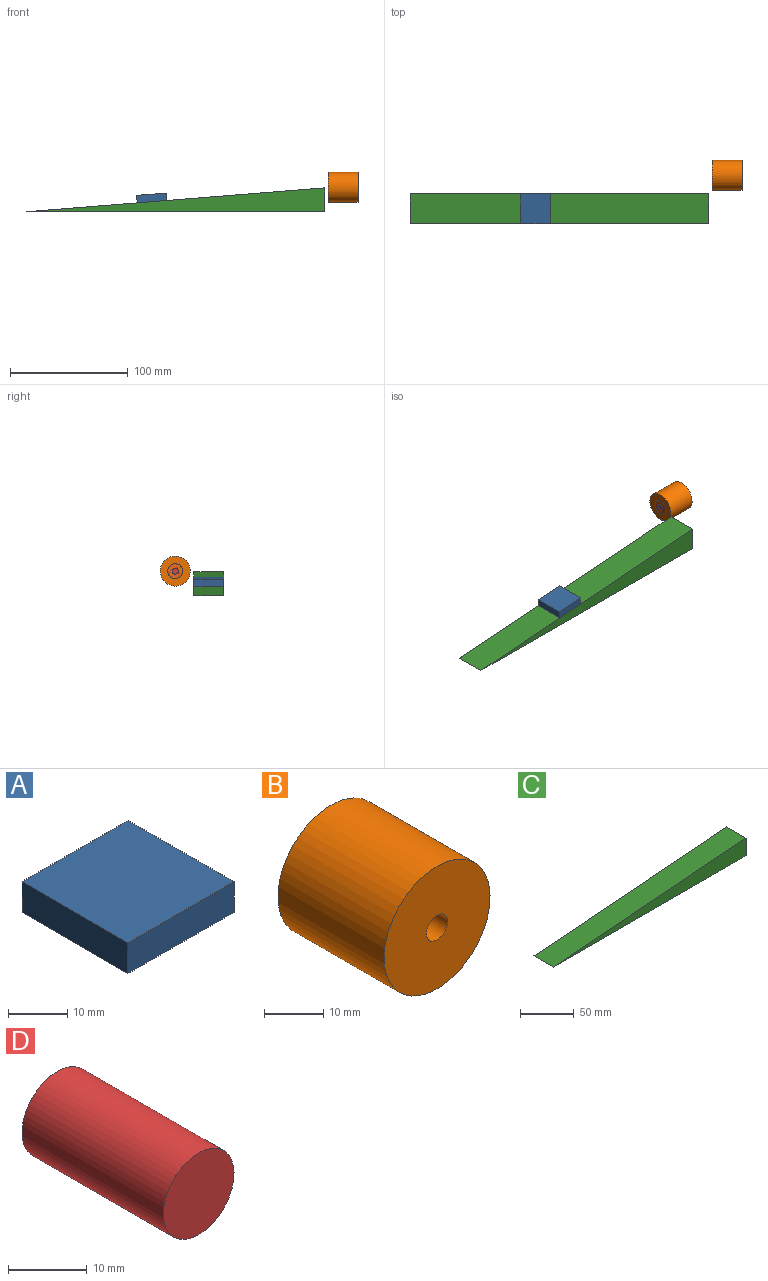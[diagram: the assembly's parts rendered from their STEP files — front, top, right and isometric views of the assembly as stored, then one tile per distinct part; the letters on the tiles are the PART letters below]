
ASSEMBLY  parts=4 mates=3
PART A: 6 faces, bbox 25.4x25.4x6.4 mm
  f0: plane 25.4x6.35mm, normal (-1,0,0), area 161.3mm2, adj f1,f3,f4,f5
  f1: plane 25.4x25.4mm, normal (0,0,-1), area 645.2mm2, adj f0,f2,f4,f5
  f2: plane 25.4x6.35mm, normal (1,0,0), area 161.3mm2, adj f1,f3,f4,f5
  f3: plane 25.4x25.4mm, normal (0,0,1), area 645.2mm2, adj f0,f2,f4,f5
  f4: plane 25.4x6.35mm, normal (0,-1,0), area 161.3mm2, adj f0,f1,f2,f3
  f5: plane 25.4x6.35mm, normal (0,1,0), area 161.3mm2, adj f0,f1,f2,f3
PART B: 4 faces, bbox 25.4x25.4x25.4 mm
  f0: cylinder r=12.7mm len=25.4mm, axis (0,1,0), area 2026.8mm2, adj f1,f2
  f1: plane 25.4x25.4mm, normal (0,-1,0), area 486.4mm2, adj f0,f3
  f2: plane 25.4x25.4mm, normal (0,1,0), area 486.4mm2, adj f0,f3
  f3: cylinder r=2.54mm len=25.4mm, axis (0,-1,0), area 405.4mm2, adj f1,f2
PART C: 5 faces, bbox 254x25.4x20.3 mm
  f0: plane 254x25.4mm, normal (-0.08,0,1), area 6472.2mm2, adj f1,f2,f3,f4
  f1: plane 254x25.4mm, normal (0,0,-1), area 6451.6mm2, adj f0,f2,f3,f4
  f2: plane 25.4x20.32mm, normal (1,0,0), area 516.1mm2, adj f0,f1,f3,f4
  f3: plane 254x20.32mm, normal (0,-1,0), area 2580.6mm2, adj f0,f1,f2
  f4: plane 254x20.32mm, normal (0,1,0), area 2580.6mm2, adj f0,f1,f2
PART D: 3 faces, bbox 12.7x25.4x12.7 mm
  f0: cylinder r=6.35mm len=25.4mm, axis (0,1,0), area 1013.4mm2, adj f1,f2
  f1: plane 12.7x12.7mm, normal (0,-1,0), area 126.7mm2, adj f0
  f2: plane 12.7x12.7mm, normal (0,1,0), area 126.7mm2, adj f0
PLACE A rot(axis=(0.04,-0.04,-1),90.1deg) t=(-146.74,-12.7,8.58)mm
PLACE B rot(axis=(0.7,0.7,-0.1),168.3deg) t=(28.43,15.77,20.9)mm
PLACE C t=(-127,0,0)mm
PLACE D rot(axis=(0.2,0.2,-0.96),92.3deg) t=(28.43,15.77,20.9)mm fixed
MATE planar A.f2 <-> C.f3  axis (0,-1,0) through (-146.99,-25.4,11.75)mm
MATE planar A.f1 <-> C.f0  axis (0.08,0,-1) through (-146.74,-12.7,8.58)mm
MATE revolute B.f0 <-> D.f0  axis (1,0,0) through (3.03,15.77,20.9)mm
